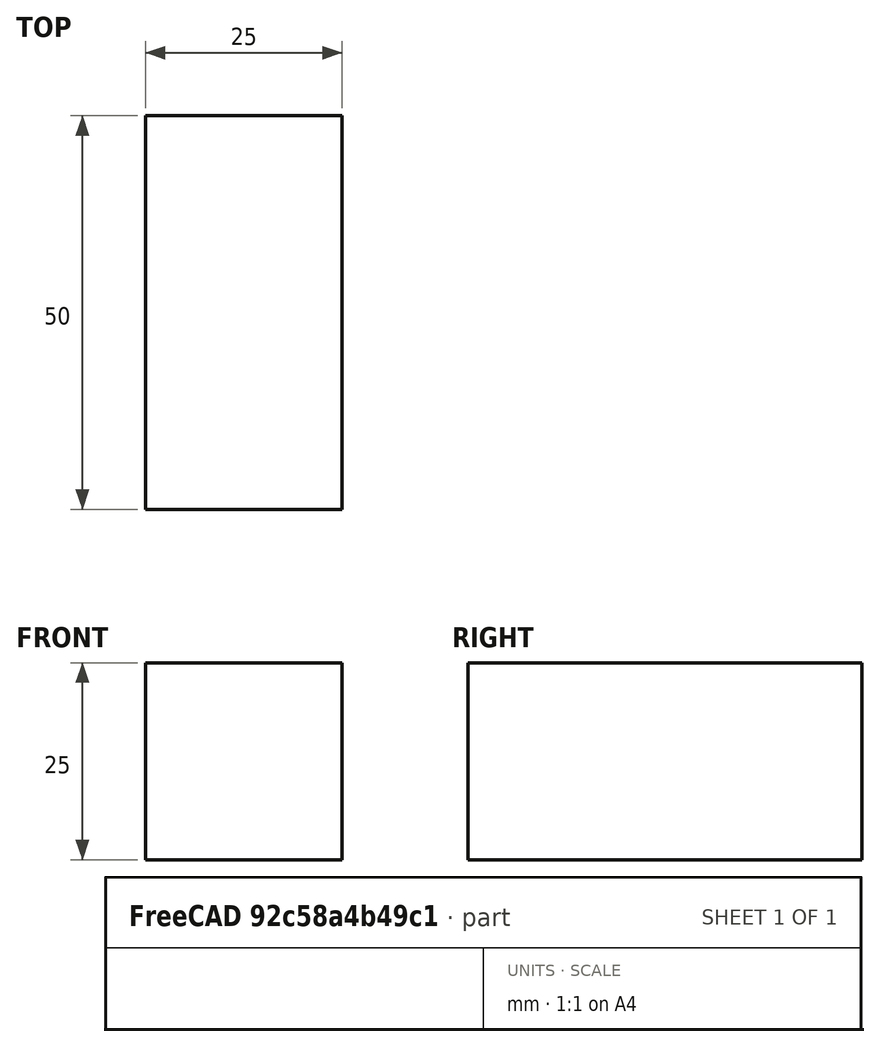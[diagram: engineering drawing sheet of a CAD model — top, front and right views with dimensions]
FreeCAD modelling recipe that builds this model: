
FCSTD DOCUMENT  (FreeCAD 1.0R39319 (Git))
Label: cube
License: All rights reserved
LicenseURL: https://en.wikipedia.org/wiki/All_rights_reserved
objects: Sketcher::SketchObject×1, Spreadsheet::Sheet×1, PartDesign::Pad×1, PartDesign::Body×1
note: 6 computed .brp shape members not serialized (recipe doc carries the construction recipe); baked Part::Feature solids carry a one-line shape summary decoded from their .brp

FEATURE [Sketcher::SketchObject] Sketch
  ArcFitTolerance = 1e-06
  AttachmentSupport = -> [XY_Plane]
  FullyConstrained = true
  MakeInternals = false
  MapMode = 5
  expr: Constraints[10] = <<dimention>>.depth
  expr: Constraints[9] = <<dimention>>.width
  sketch-geometry (4):
    g0: LineSegment StartX=0 StartY=0 StartZ=0 EndX=25 EndY=0 EndZ=0
    g1: LineSegment StartX=25 StartY=0 StartZ=0 EndX=25 EndY=50 EndZ=0
    g2: LineSegment StartX=25 StartY=50 StartZ=0 EndX=0 EndY=50 EndZ=0
    g3: LineSegment StartX=0 StartY=50 StartZ=0 EndX=0 EndY=0 EndZ=0
  constraints (11):
    c: Coincident(g0,g1)
    c: Coincident(g1,g2)
    c: Coincident(g2,g3)
    c: Coincident(g3,g0)
    c: Horizontal(g0)
    c: Horizontal(g2)
    c: Vertical(g1)
    c: Vertical(g3)
    c: Coincident(g0,g-1)
    c: DistanceX(g0,g0) = 25
    c: DistanceY(g3,g3) = 50
FEATURE [Spreadsheet::Sheet] Spreadsheet  label="dimention"
  cells = A1='幅; B1(width)==25 mm; A2='奥行き; B2(depth)==50 mm; A3='高さ; B3(height)==25 mm
FEATURE [PartDesign::Pad] Pad
  Direction = (0,0,1)
  Length = 25
  Length2 = 10
  Profile = -> Sketch
  ReferenceAxis = -> Sketch [N_Axis]
  Refine = true
  Suppressed = false
  Type = 0
  expr: Length = <<dimention>>.height
FEATURE [PartDesign::Body] Body
  AllowCompound = false
  Group = -> [Sketch,Pad]
  Origin = -> Origin
  Tip = -> Pad
